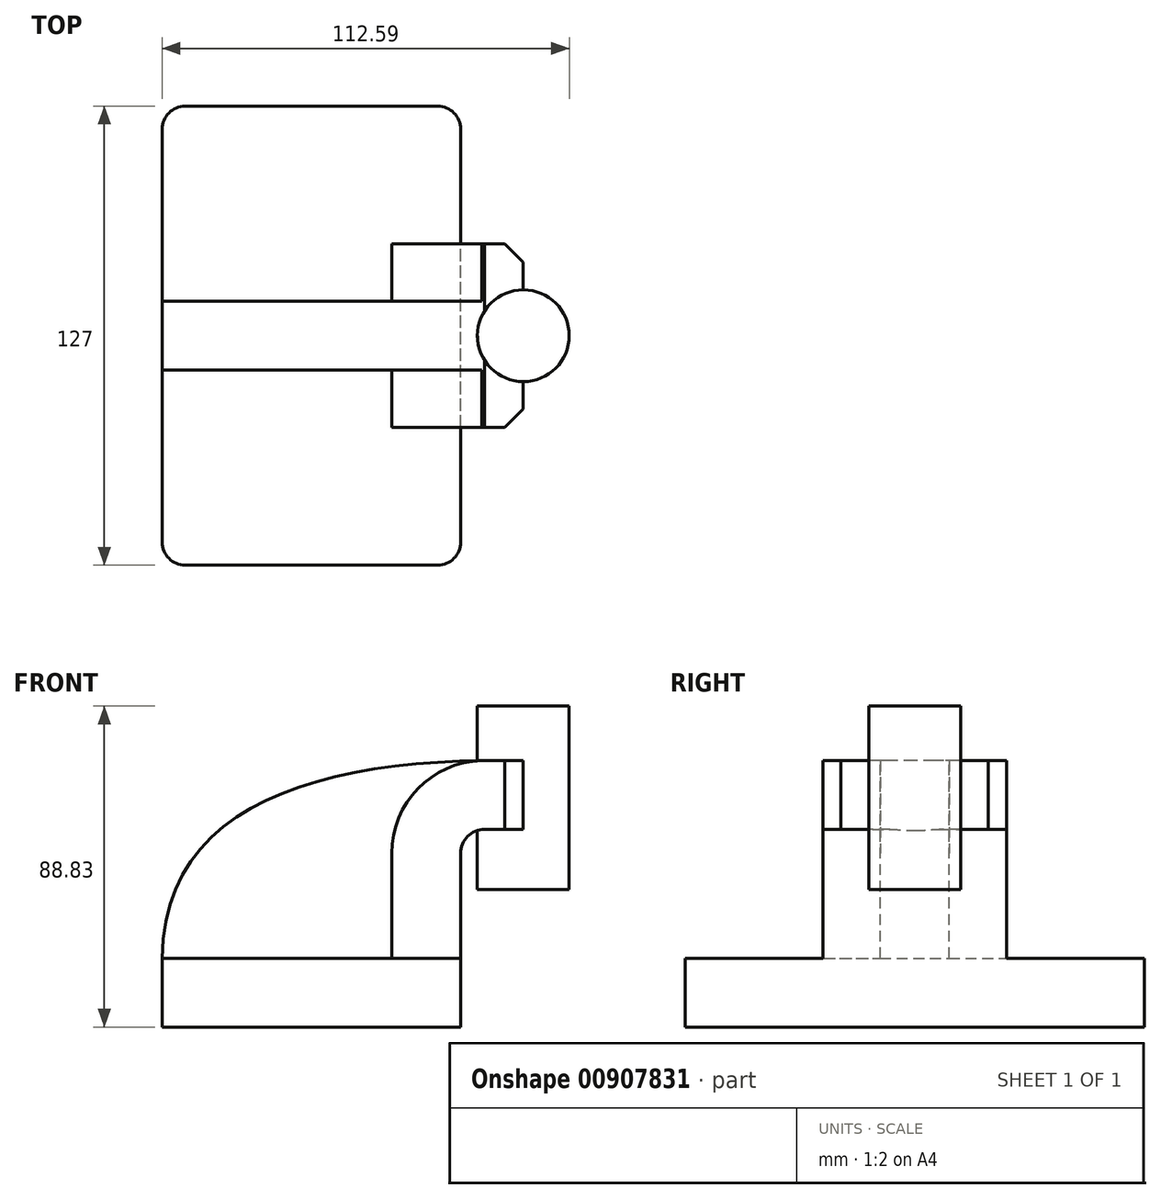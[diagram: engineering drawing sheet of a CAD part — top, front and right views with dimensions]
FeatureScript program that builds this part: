
annotation { "Feature Type Name" : "Feature", "Feature Type Description" : "" }
export const myFeature = defineFeature(function(context is Context, id is Id, definition is map)
    precondition{}
    {
        {
            var Q0;
            Q0=qCreatedBy(makeId("Front.planeOp"),FACE);
            var sketch = newSketch(context, id + "F0", { "sketchPlane" : qUnion([Q0])});
            skLineSegment(sketch, "E0.bottom", {"start": v(41.28, -9.52) * mm, "end": v(-41.27, -9.53) * mm});
            skLineSegment(sketch, "E0.top", {"start": v(41.27, 9.53) * mm, "end": v(-41.28, 9.53) * mm});
            skLineSegment(sketch, "E0.left", {"start": v(41.28, -9.52) * mm, "end": v(41.28, 9.53) * mm});
            skLineSegment(sketch, "E0.right", {"start": v(-41.27, -9.52) * mm, "end": v(-41.28, 9.53) * mm});
            skPoint(sketch, "E0.middle", {"position": v(0, 0) * mm});
            skLineSegment(sketch, "E1.bottom", {"start": v(84, 28.5) * mm, "end": v(58.6, 28.5) * mm});
            skLineSegment(sketch, "E1.top", {"start": v(84, 79.3) * mm, "end": v(58.6, 79.3) * mm});
            skLineSegment(sketch, "E1.left", {"start": v(84, 28.5) * mm, "end": v(84, 79.3) * mm});
            skLineSegment(sketch, "E1.right", {"start": v(58.6, 28.5) * mm, "end": v(58.6, 79.3) * mm});
            skPoint(sketch, "E1.middle", {"position": v(71.3, 53.9) * mm});
            skLineSegment(sketch, "E2", {"start": v(41.27, 9.53) * mm, "end": v(41.27, 38.54) * mm});
            skArc(sketch, "E3", {"start": v(41.27, 38.54) * mm, "mid": v(43.22, 43.24) * mm, "end": v(47.91, 45.18) * mm});
            skLineSegment(sketch, "E4", {"start": v(47.91, 45.18) * mm, "end": v(71.3, 45.18) * mm});
            skLineSegment(sketch, "E5.0", {"start": v(47.91, 64.23) * mm, "end": v(71.3, 64.23) * mm});
            skArc(sketch, "E5.1", {"start": v(22.22, 38.54) * mm, "mid": v(29.75, 56.7) * mm, "end": v(47.91, 64.23) * mm});
            skLineSegment(sketch, "E5.2", {"start": v(22.22, 9.53) * mm, "end": v(22.22, 38.54) * mm});
            skLineSegment(sketch, "E6", {"start": v(71.3, 28.5) * mm, "end": v(71.3, 79.3) * mm});
            skFitSpline(sketch, "E7", {"points": [v(-41.28, 9.53) * mm, v(47.91, 64.23) * mm], "startDerivative": vector(1.33, 124.72) * mm, "endDerivative": vector(143.73, 2) * mm});
            skSolve(sketch);
        }
        {
            var Q0;
            Q0=makeQuery(id+"F0.imprint","IMPRINT",FACE,{"disambiguationData":[TD([[makeQuery(id+"F0.imprint","IMPRINT",EDGE,{"derivedFrom":sQuery(id+"F0.wireOp",EDGE,"E0.bottom")}),-1.0]])]});
            extrude(context, id + "F1", {"entities" : qUnion([Q0]), "endBound" : BoundingType.SYMMETRIC, "depth" : 127 * mm});
        }
        {
            var Q0;
            {var subQ1=sQuery(id+"F0.wireOp",EDGE,"E2");Q0=makeQuery(id+"F0.imprint","IMPRINT",FACE,{"disambiguationData":[TD([[makeQuery(id+"F0.imprint","IMPRINT",EDGE,{"derivedFrom":subQ1}),1.0]])]});}
            extrude(context, id + "F2", {"entities" : qUnion([Q0]), "operationType" : NewBodyOperationType.ADD, "endBound" : BoundingType.SYMMETRIC, "depth" : 50.8 * mm});
        }
        {
            var Q0;
            {var subQ3=sQuery(id+"F0.wireOp",EDGE,"E5.2");Q0=makeQuery(id+"F0.imprint","IMPRINT",FACE,{"disambiguationData":[TD([[makeQuery(id+"F0.imprint","IMPRINT",EDGE,{"derivedFrom":subQ3}),1.0]])]});}
            extrude(context, id + "F3", {"entities" : qUnion([Q0]), "operationType" : NewBodyOperationType.ADD, "endBound" : BoundingType.SYMMETRIC, "depth" : 19.05 * mm});
        }
        {
            var Q0;
            {var subQ0=sQuery(id+"F0.wireOp",EDGE,"E4");var subQ1=sQuery(id+"F0.wireOp",EDGE,"E1.right");var subQ2=makeQuery(id+"F0.imprint","INTERSECT",VERTEX,{"derivedFrom":[subQ1,subQ0]});Q0=makeQuery(id+"F0.imprint","IMPRINT",FACE,{"disambiguationData":[TD([[makeQuery(id+"F0.imprint","IMPRINT",EDGE,{"disambiguationData":[TD([[subQ2,-1.0]])],"derivedFrom":subQ1}),-1.0]])]});}
            var Q1;
            {var subQ0=sQuery(id+"F0.wireOp",EDGE,"E1.right");var subQ1=sQuery(id+"F0.wireOp",EDGE,"E1.top");var subQ2=makeQuery(id+"F0.imprint","INTERSECT",VERTEX,{"derivedFrom":[subQ1,subQ0]});Q1=makeQuery(id+"F0.imprint","IMPRINT",FACE,{"disambiguationData":[TD([[makeQuery(id+"F0.imprint","IMPRINT",EDGE,{"disambiguationData":[TD([[subQ2,1.0]])],"derivedFrom":subQ1}),1.0]])]});}
            var Q2;
            {var subQ0=sQuery(id+"F0.wireOp",EDGE,"E1.right");var subQ1=sQuery(id+"F0.wireOp",EDGE,"E1.bottom");var subQ2=makeQuery(id+"F0.imprint","INTERSECT",VERTEX,{"derivedFrom":[subQ1,subQ0]});Q2=makeQuery(id+"F0.imprint","IMPRINT",FACE,{"disambiguationData":[TD([[makeQuery(id+"F0.imprint","IMPRINT",EDGE,{"disambiguationData":[TD([[subQ2,1.0]])],"derivedFrom":subQ1}),-1.0]])]});}
            var Q3;
            Q3=sQuery(id+"F0.wireOp",EDGE,"E1.right");
            revolve(context, id + "F4", {"operationType" : NewBodyOperationType.ADD, "entities" : qUnion([Q0, Q1, Q2]), "axis" : qUnion([Q3]), "revolveType" : RevolveType.FULL});
        }
        {
            var Q0;
            Q0=makeQuery(id+"F1.opExtrude","CAP_EDGE",EDGE,{"disambiguationData":[OSD([sQuery(id+"F0.wireOp",EDGE,"E0.right")])],"isStart":false});
            var Q1;
            Q1=makeQuery(id+"F1.opExtrude","CAP_EDGE",EDGE,{"disambiguationData":[OSD([sQuery(id+"F0.wireOp",EDGE,"E0.left")])],"isStart":false});
            var Q2;
            Q2=makeQuery(id+"F1.opExtrude","CAP_EDGE",EDGE,{"disambiguationData":[OSD([sQuery(id+"F0.wireOp",EDGE,"E0.right")])],"isStart":true});
            var Q3;
            Q3=makeQuery(id+"F1.opExtrude","CAP_EDGE",EDGE,{"disambiguationData":[OSD([sQuery(id+"F0.wireOp",EDGE,"E0.left")])],"isStart":true});
            fillet(context, id + "F5", {"entities" : qUnion([Q0, Q1, Q2, Q3]), "radius" : 6.35 * mm, "tangentPropagation" : true, "allowEdgeOverflow" : false});
        }
        {
            var Q0;
            Q0=makeQuery(id+"F2.opExtrude","CAP_EDGE",EDGE,{"disambiguationData":[OSD([sQuery(id+"F0.wireOp",EDGE,"E1.right")])],"isStart":false});
            var Q1;
            Q1=makeQuery(id+"F2.opExtrude","CAP_EDGE",EDGE,{"disambiguationData":[OSD([sQuery(id+"F0.wireOp",EDGE,"E1.right")])],"isStart":true});
            chamfer(context, id + "F6", {"entities" : qUnion([Q0, Q1]), "width" : 5.08 * mm, "tangentPropagation" : true});
        }
    });
